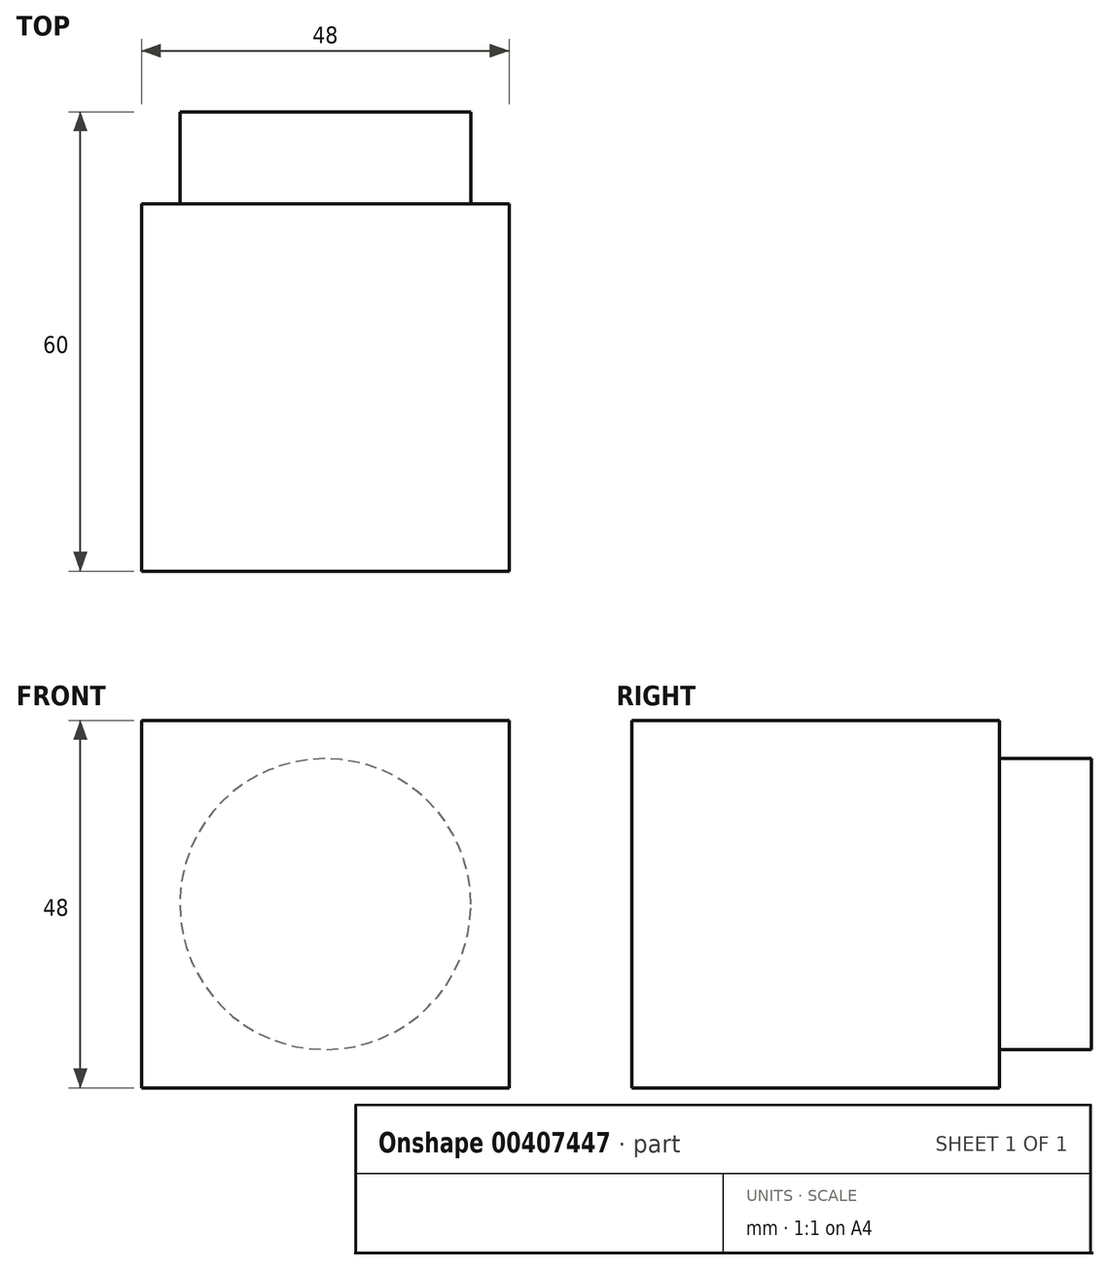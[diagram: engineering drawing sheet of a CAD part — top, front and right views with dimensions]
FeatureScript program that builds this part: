
annotation { "Feature Type Name" : "Feature", "Feature Type Description" : "" }
export const myFeature = defineFeature(function(context is Context, id is Id, definition is map)
    precondition{}
    {
        {
            var Q0;
            Q0=qCreatedBy(makeId("Front.planeOp"),FACE);
            var sketch = newSketch(context, id + "F0", { "sketchPlane" : qUnion([Q0])});
            skLineSegment(sketch, "E0.bottom", {"start": v(-24, 24) * mm, "end": v(24, 24) * mm});
            skLineSegment(sketch, "E0.top", {"start": v(-24, -24) * mm, "end": v(24, -24) * mm});
            skLineSegment(sketch, "E0.left", {"start": v(-24, 24) * mm, "end": v(-24, -24) * mm});
            skLineSegment(sketch, "E0.right", {"start": v(24, 24) * mm, "end": v(24, -24) * mm});
            skPoint(sketch, "E0.middle", {"position": v(0, 0) * mm});
            skSolve(sketch);
        }
        {
            var Q0;
            Q0 = qSketchRegion(id + "F0", true);
            extrude(context, id + "F1", {"entities" : qUnion([Q0]), "depth" : 48 * mm});
        }
        {
            var Q0;
            Q0=qCreatedBy(makeId("Front.planeOp"),FACE);
            var sketch = newSketch(context, id + "F2", { "sketchPlane" : qUnion([Q0])});
            skCircle(sketch, "E1", {"center": v(-11.59, 11.3) * mm, "radius": 8 * mm});
            skCircle(sketch, "E2", {"center": v(11.89, 11.3) * mm, "radius": 8 * mm});
            skCircle(sketch, "E3", {"center": v(11.89, -11.59) * mm, "radius": 8 * mm});
            skCircle(sketch, "E4", {"center": v(-11.59, -11.59) * mm, "radius": 8 * mm});
            skSolve(sketch);
        }
        {
            var Q0;
            Q0 = qSketchRegion(id + "F2", true);
            extrude(context, id + "F3", {"entities" : qUnion([Q0]), "operationType" : NewBodyOperationType.ADD, "depth" : 7 * mm, "hasDraft" : true, "draftAngle" : 3 * degree});
        }
        {
            var Q0;
            Q0=qCreatedBy(makeId("Front.planeOp"),FACE);
            var sketch = newSketch(context, id + "F4", { "sketchPlane" : qUnion([Q0])});
            skCircle(sketch, "E5", {"center": v(0, 0) * mm, "radius": 19 * mm});
            skSolve(sketch);
        }
        {
            var Q0;
            Q0 = qSketchRegion(id + "F4", true);
            var Q1;
            Q1 = qConstructionFilter(qBodyType(qCreatedBy(id + "F4" ,EDGE), BodyType.WIRE), ConstructionObject.NO);
            extrude(context, id + "F5", {"entities" : qUnion([Q0]), "operationType" : NewBodyOperationType.ADD, "surfaceEntities" : qUnion([Q1]), "oppositeDirection" : true, "depth" : 12 * mm});
        }
    });
